# Revit family: Gira_209700
name_source: partatom
category: Electrical Fixtures
revit_build: Autodesk Revit 2017 (Build: 20160225_1515(x64)
units: mm (PartAtom-declared; Revit-internal decimal feet)

## family parameters
Cut with Voids When Loaded = No
Host = Face
Maintain Annotation Orientation = Yes
Part Type = Normal
Room Calculation Point = No
Round Connector Dimension = Use Diameter
Shared = No

## types (1)
- Gira Control 9 Client 2 Elektronik
    Andere Bussysteme = ohne
    Available = Yes
    Bussystem Funkbus = No
    Bussystem KNX = Yes
    Bussystem KNX-Funk = No
    Bussystem LON = No
    Bussystem Powernet = No
    Category = Bussystem-Mehrfach Bediengerät
    DCF77 Empfänger integriert = No
    Data sheet (1) = https://katalog.gira.de
    Default Elevation = 1219 mm
    Funk bidirektional = No
    GTIN = 4010337029267
    HAN = 209700
    HeinzeBIM = https://bimportal.heinze.de
    IR-Sensor = No
    Keynote = GiraHomeServer_GC9 Client
    Manuelle Sollwertverstellung = Yes
    Manufacturer URL = https://www.gira.de
    Mit Busankopplung = Yes
    Mit Diebstahl-/Demontageschutz = No
    Mit Display = Yes
    Montageart = unter Putz
    Name = Gira Control 9 Client 2 Elektronik
    Präsenztaster = No
    Region = DE
    Schutzart (IP) = IP20
    Status-LED = No
    Temperaturregler = Yes
    URL = http://katalog.gira.de
    Zentrale Funktionseinheit für Sender/Aktoren = Yes

## geometry (parser evidence)
native form markers: Blend x2, Sweep x2
no freeform markers — native parametric forms only
